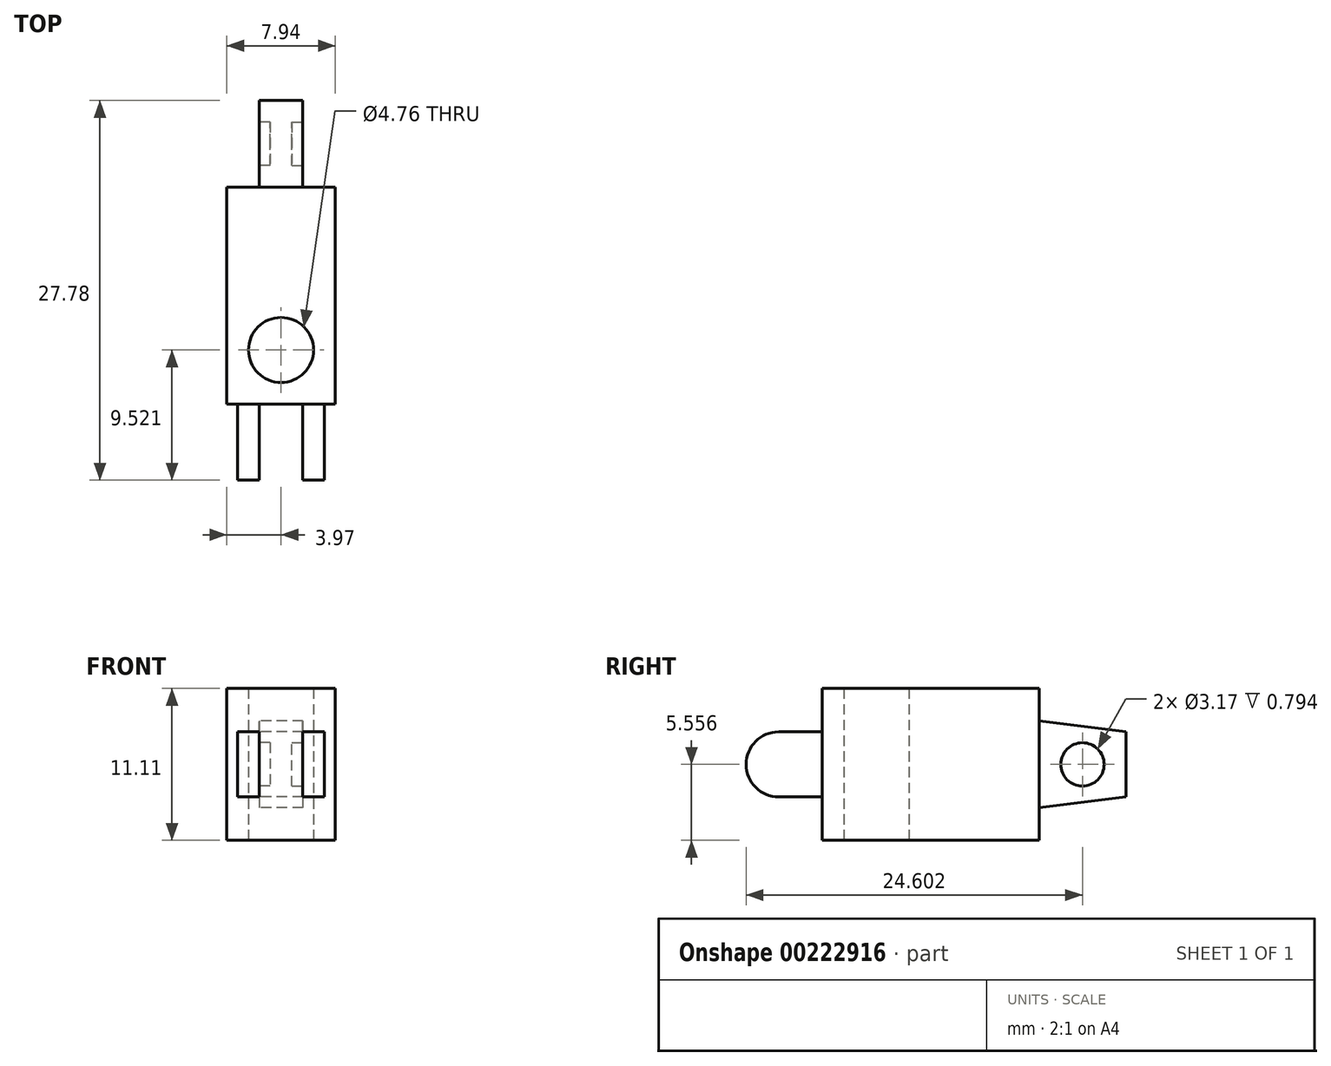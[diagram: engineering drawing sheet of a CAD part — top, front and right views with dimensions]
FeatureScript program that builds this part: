
annotation { "Feature Type Name" : "Feature", "Feature Type Description" : "" }
export const myFeature = defineFeature(function(context is Context, id is Id, definition is map)
    precondition{}
    {
        {
            var Q0;
            Q0=qCreatedBy(makeId("Top.planeOp"),FACE);
            var sketch = newSketch(context, id + "F0", { "sketchPlane" : qUnion([Q0])});
            skLineSegment(sketch, "E0.bottom", {"start": v(-3.97, 7.94) * mm, "end": v(3.97, 7.94) * mm});
            skLineSegment(sketch, "E0.top", {"start": v(-3.97, -7.94) * mm, "end": v(3.97, -7.94) * mm});
            skLineSegment(sketch, "E0.left", {"start": v(-3.97, 7.94) * mm, "end": v(-3.97, -7.94) * mm});
            skLineSegment(sketch, "E0.right", {"start": v(3.97, 7.94) * mm, "end": v(3.97, -7.94) * mm});
            skPoint(sketch, "E0.middle", {"position": v(0, 0) * mm});
            skCircle(sketch, "E1", {"center": v(0, 3.97) * mm, "radius": 2.38 * mm});
            skCircle(sketch, "E2.MirrorC", {"center": v(0, -3.97) * mm, "radius": 2.38 * mm});
            skSolve(sketch);
        }
        {
            var Q0;
            Q0 = qSketchRegion(id + "F0", true);
            extrude(context, id + "F1", {"entities" : qUnion([Q0]), "depth" : 9.52 * mm});
        }
        {
            var Q0;
            Q0=makeQuery(id+"F0.imprint","IMPRINT",FACE,{"disambiguationData":[TD([[makeQuery(id+"F0.imprint","IMPRINT",EDGE,{"derivedFrom":sQuery(id+"F0.wireOp",EDGE,"E1")}),1.0]])]});
            var Q1;
            Q1=makeQuery(id+"F0.imprint","IMPRINT",FACE,{"disambiguationData":[TD([[makeQuery(id+"F0.imprint","IMPRINT",EDGE,{"derivedFrom":sQuery(id+"F0.wireOp",EDGE,"E2.MirrorC")}),-1.0]])]});
            extrude(context, id + "F2", {"entities" : qUnion([Q0, Q1]), "operationType" : NewBodyOperationType.ADD, "depth" : 11.1 * mm});
        }
        {
            var Q0;
            Q0=qCreatedBy(makeId("Right.planeOp"),FACE);
            var sketch = newSketch(context, id + "F3", { "sketchPlane" : qUnion([Q0])});
            skLineSegment(sketch, "E3", {"start": v(0, 5.56) * mm, "end": v(-7.94, 5.56) * mm});
            skLineSegment(sketch, "E4", {"start": v(-7.94, 5.56) * mm, "end": v(-7.94, 7.94) * mm});
            skLineSegment(sketch, "E5.bottom", {"start": v(-7.94, 7.94) * mm, "end": v(-11.11, 7.94) * mm});
            skLineSegment(sketch, "E5.top", {"start": v(-7.94, 5.56) * mm, "end": v(-11.11, 5.56) * mm});
            skLineSegment(sketch, "E5.left", {"start": v(-7.94, 7.94) * mm, "end": v(-7.94, 5.56) * mm});
            skLineSegment(sketch, "E5.right", {"start": v(-11.11, 7.94) * mm, "end": v(-11.11, 5.56) * mm});
            skLineSegment(sketch, "E6.MirrorCS", {"start": v(-11.11, 3.17) * mm, "end": v(-11.11, 5.56) * mm});
            skLineSegment(sketch, "E7.MirrorCS", {"start": v(-7.94, 3.17) * mm, "end": v(-11.11, 3.17) * mm});
            skLineSegment(sketch, "E8.MirrorCS", {"start": v(-7.94, 3.17) * mm, "end": v(-7.94, 5.56) * mm});
            skLineSegment(sketch, "E9", {"start": v(-11.11, 5.56) * mm, "end": v(-13.5, 5.56) * mm});
            skArc(sketch, "E10", {"start": v(-11.11, 7.94) * mm, "mid": v(-13.5, 5.56) * mm, "end": v(-11.11, 3.17) * mm});
            skLineSegment(sketch, "E11", {"start": v(0, 5.56) * mm, "end": v(7.94, 5.56) * mm});
            skLineSegment(sketch, "E12", {"start": v(7.94, 5.56) * mm, "end": v(14.29, 5.56) * mm});
            skLineSegment(sketch, "E13", {"start": v(14.29, 5.56) * mm, "end": v(14.29, 7.94) * mm});
            skLineSegment(sketch, "E14", {"start": v(14.29, 7.94) * mm, "end": v(7.94, 8.73) * mm});
            skLineSegment(sketch, "E15", {"start": v(7.94, 8.73) * mm, "end": v(7.94, 5.56) * mm});
            skLineSegment(sketch, "E16.MirrorCS", {"start": v(14.29, 5.56) * mm, "end": v(14.29, 3.18) * mm});
            skLineSegment(sketch, "E17.MirrorCS", {"start": v(14.29, 3.18) * mm, "end": v(7.94, 2.38) * mm});
            skLineSegment(sketch, "E18.MirrorCS", {"start": v(7.94, 2.38) * mm, "end": v(7.94, 5.56) * mm});
            skSolve(sketch);
        }
        {
            var Q0;
            Q0=makeQuery(id+"F3.imprint","IMPRINT",FACE,{"disambiguationData":[TD([[makeQuery(id+"F3.imprint","IMPRINT",EDGE,{"derivedFrom":sQuery(id+"F3.wireOp",EDGE,"E5.bottom")}),1.0]])]});
            var Q1;
            Q1=makeQuery(id+"F3.imprint","IMPRINT",FACE,{"disambiguationData":[TD([[makeQuery(id+"F3.imprint","IMPRINT",EDGE,{"derivedFrom":sQuery(id+"F3.wireOp",EDGE,"E5.top")}),1.0]])]});
            var Q2;
            {var subQ0=sQuery(id+"F3.wireOp",EDGE,"E5.right");Q2=makeQuery(id+"F3.imprint","IMPRINT",FACE,{"disambiguationData":[TD([[makeQuery(id+"F3.imprint","IMPRINT",EDGE,{"derivedFrom":subQ0}),-1.0]])]});}
            var Q3;
            {var subQ0=sQuery(id+"F3.wireOp",EDGE,"E6.MirrorCS");Q3=makeQuery(id+"F3.imprint","IMPRINT",FACE,{"disambiguationData":[TD([[makeQuery(id+"F3.imprint","IMPRINT",EDGE,{"derivedFrom":subQ0}),1.0]])]});}
            extrude(context, id + "F4", {"entities" : qUnion([Q0, Q1, Q2, Q3]), "operationType" : NewBodyOperationType.ADD, "endBound" : BoundingType.SYMMETRIC, "depth" : 6.35 * mm});
        }
        {
            var Q0;
            Q0=makeQuery(id+"F4.opExtrude","SWEPT_FACE",FACE,{"disambiguationData":[OSD([sQuery(id+"F3.wireOp",EDGE,"E5.bottom")])]});
            var sketch = newSketch(context, id + "F5", { "sketchPlane" : qUnion([Q0])});
            skLineSegment(sketch, "E19", {"start": v(0, -7.94) * mm, "end": v(0, -14.29) * mm});
            skPoint(sketch, "E19.endSnap0", {"position": v(0, -11.11) * mm});
            skLineSegment(sketch, "E20", {"start": v(0, -14.29) * mm, "end": v(-1.59, -14.29) * mm});
            skLineSegment(sketch, "E21", {"start": v(-1.59, -14.29) * mm, "end": v(-1.59, -7.94) * mm});
            skLineSegment(sketch, "E22", {"start": v(-1.59, -7.94) * mm, "end": v(0, -7.94) * mm});
            skLineSegment(sketch, "E23.MirrorCS", {"start": v(1.59, -7.94) * mm, "end": v(0, -7.94) * mm});
            skLineSegment(sketch, "E24.MirrorCS", {"start": v(1.59, -14.29) * mm, "end": v(1.59, -7.94) * mm});
            skLineSegment(sketch, "E25.MirrorCS", {"start": v(0, -14.29) * mm, "end": v(1.59, -14.29) * mm});
            skSolve(sketch);
        }
        {
            var Q0;
            Q0 = qSketchRegion(id + "F5", true);
            extrude(context, id + "F6", {"entities" : qUnion([Q0]), "operationType" : NewBodyOperationType.REMOVE, "oppositeDirection" : true, "depth" : 6.35 * mm});
        }
        {
            var Q0;
            Q0=makeQuery(id+"F3.imprint","IMPRINT",FACE,{"disambiguationData":[TD([[makeQuery(id+"F3.imprint","IMPRINT",EDGE,{"derivedFrom":sQuery(id+"F3.wireOp",EDGE,"E12")}),1.0]])]});
            var Q1;
            Q1=makeQuery(id+"F3.imprint","IMPRINT",FACE,{"disambiguationData":[TD([[makeQuery(id+"F3.imprint","IMPRINT",EDGE,{"derivedFrom":sQuery(id+"F3.wireOp",EDGE,"E12")}),-1.0]])]});
            extrude(context, id + "F7", {"entities" : qUnion([Q0, Q1]), "operationType" : NewBodyOperationType.ADD, "endBound" : BoundingType.SYMMETRIC, "depth" : 3.17 * mm});
        }
        {
            var Q0;
            Q0=makeQuery(id+"F7.opExtrude","CAP_FACE",FACE,{"disambiguationData":[OSD([sQuery(id+"F3.wireOp",EDGE,"E13"),sQuery(id+"F3.wireOp",EDGE,"E14"),sQuery(id+"F3.wireOp",EDGE,"E15"),sQuery(id+"F3.wireOp",EDGE,"E16.MirrorCS"),sQuery(id+"F3.wireOp",EDGE,"E17.MirrorCS"),sQuery(id+"F3.wireOp",EDGE,"E18.MirrorCS")])],"isStart":false});
            var sketch = newSketch(context, id + "F8", { "sketchPlane" : qUnion([Q0])});
            skCircle(sketch, "E26", {"center": v(11.11, 5.56) * mm, "radius": 1.59 * mm});
            skPoint(sketch, "E26.centerSnap0", {"position": v(14.29, 5.56) * mm});
            skSolve(sketch);
        }
        {
            var Q0;
            Q0 = qSketchRegion(id + "F8", true);
            extrude(context, id + "F9", {"entities" : qUnion([Q0]), "operationType" : NewBodyOperationType.REMOVE, "oppositeDirection" : true, "depth" : 0.8 * mm});
        }
        {
            var Q0;
            Q0=makeQuery(id+"F7.opExtrude","CAP_FACE",FACE,{"disambiguationData":[OSD([sQuery(id+"F3.wireOp",EDGE,"E13"),sQuery(id+"F3.wireOp",EDGE,"E14"),sQuery(id+"F3.wireOp",EDGE,"E15"),sQuery(id+"F3.wireOp",EDGE,"E16.MirrorCS"),sQuery(id+"F3.wireOp",EDGE,"E17.MirrorCS"),sQuery(id+"F3.wireOp",EDGE,"E18.MirrorCS")])],"isStart":true});
            var sketch = newSketch(context, id + "F10", { "sketchPlane" : qUnion([Q0])});
            skCircle(sketch, "E27", {"center": v(-11.11, 5.56) * mm, "radius": 1.59 * mm});
            skSolve(sketch);
        }
        {
            var Q0;
            Q0 = qSketchRegion(id + "F10", true);
            extrude(context, id + "F11", {"entities" : qUnion([Q0]), "operationType" : NewBodyOperationType.REMOVE, "oppositeDirection" : true, "depth" : 0.8 * mm});
        }
    });
